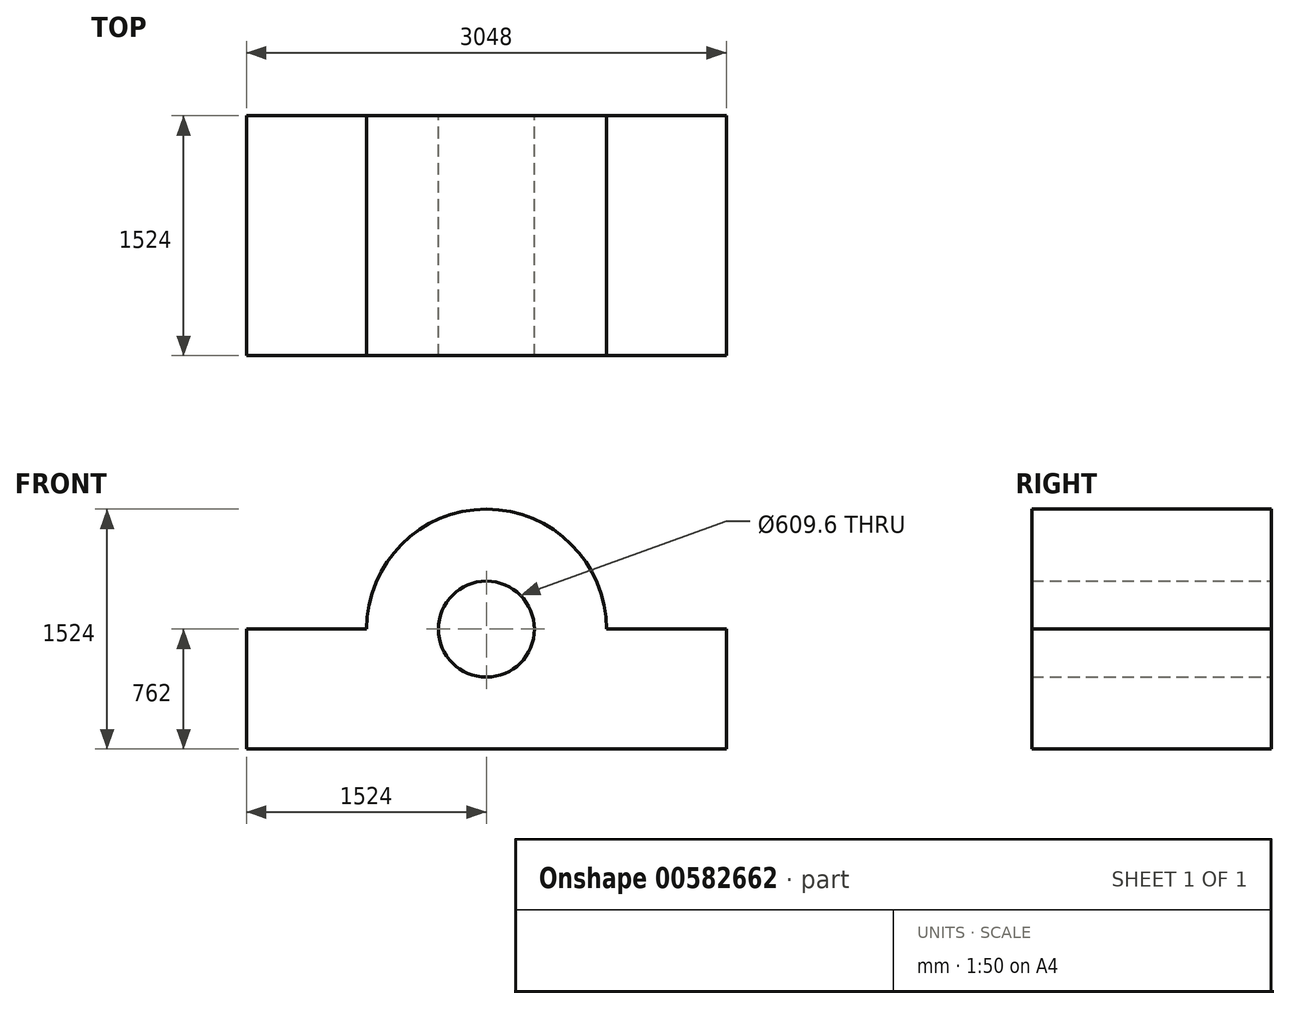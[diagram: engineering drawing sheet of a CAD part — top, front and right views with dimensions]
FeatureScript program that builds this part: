
annotation { "Feature Type Name" : "Feature", "Feature Type Description" : "" }
export const myFeature = defineFeature(function(context is Context, id is Id, definition is map)
    precondition{}
    {
        {
            var Q0;
            Q0=qCreatedBy(makeId("Front.planeOp"),FACE);
            var sketch = newSketch(context, id + "F0", { "sketchPlane" : qUnion([Q0])});
            skLineSegment(sketch, "E0", {"start": v(0, 0) * mm, "end": v(3048, 0) * mm});
            skLineSegment(sketch, "E1", {"start": v(3048, 0) * mm, "end": v(3048, 762) * mm});
            skLineSegment(sketch, "E2", {"start": v(0, 0) * mm, "end": v(0, 762) * mm});
            skCircle(sketch, "E3", {"center": v(1524, 762) * mm, "radius": 304.8 * mm});
            skPoint(sketch, "E3.centerSnap0", {"position": v(1524, 0) * mm});
            skLineSegment(sketch, "E4", {"start": v(0, 762) * mm, "end": v(762, 762) * mm});
            skLineSegment(sketch, "E5", {"start": v(3048, 762) * mm, "end": v(2286, 762) * mm});
            skArc(sketch, "E6", {"start": v(2286, 762) * mm, "mid": v(1524, 1524) * mm, "end": v(762, 762) * mm});
            skSolve(sketch);
        }
        {
            var Q0;
            Q0 = qSketchRegion(id + "F0", true);
            extrude(context, id + "F1", {"entities" : qUnion([Q0]), "depth" : 1524 * mm, "offsetDistance" : 25.4 * mm});
        }
    });
